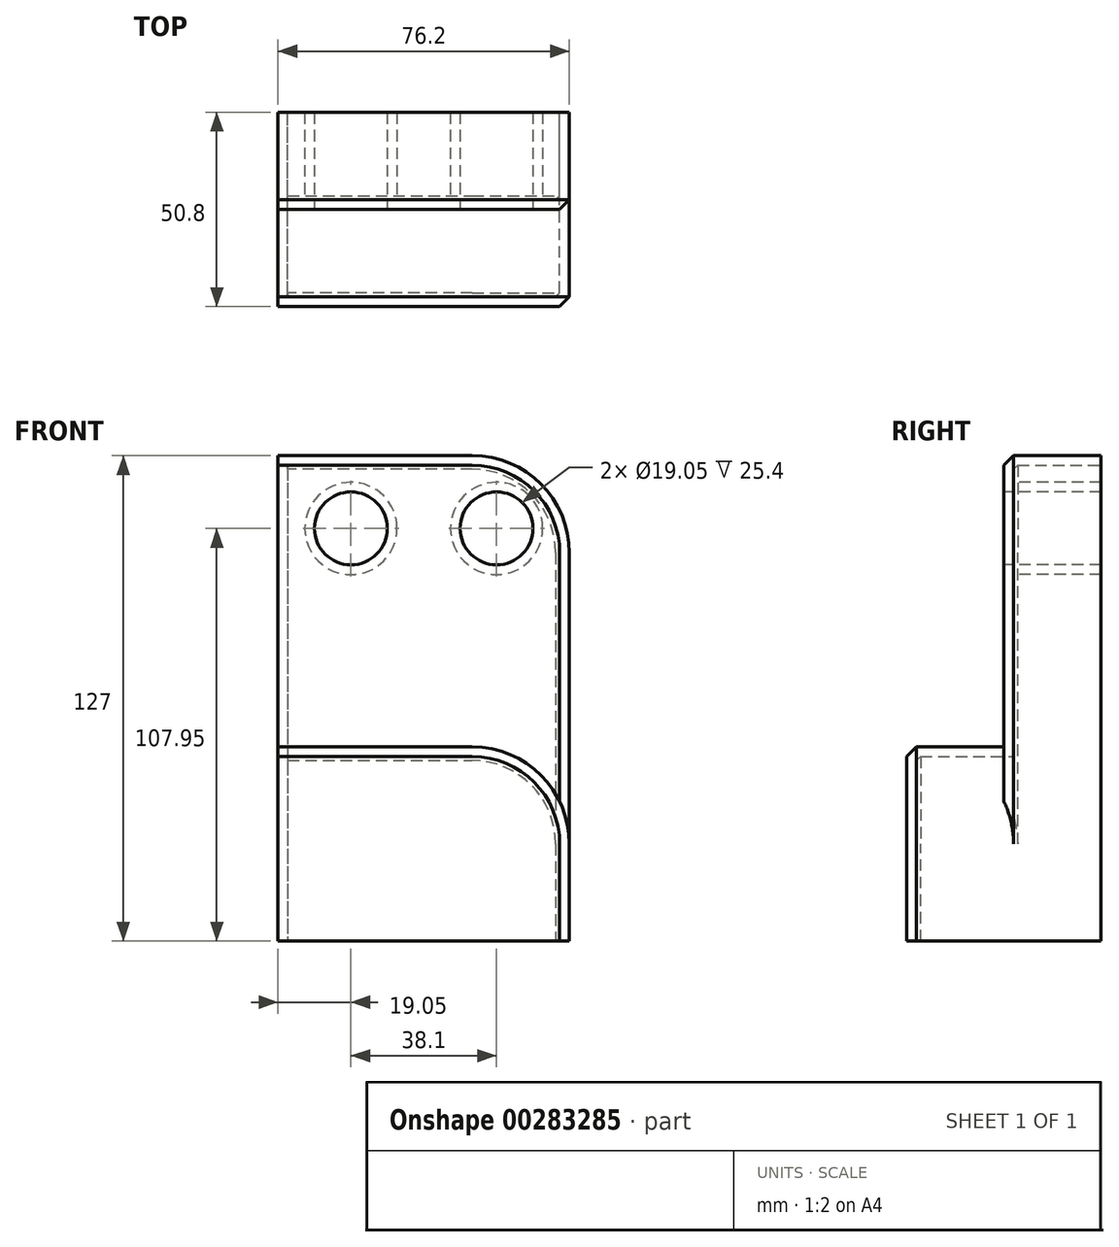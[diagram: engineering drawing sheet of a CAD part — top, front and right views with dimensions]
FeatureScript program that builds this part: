
annotation { "Feature Type Name" : "Feature", "Feature Type Description" : "" }
export const myFeature = defineFeature(function(context is Context, id is Id, definition is map)
    precondition{}
    {
        {
            var Q0;
            Q0=qCreatedBy(makeId("Front.planeOp"),FACE);
            var sketch = newSketch(context, id + "F0", { "sketchPlane" : qUnion([Q0])});
            skLineSegment(sketch, "E0.bottom", {"start": v(38.1, 63.5) * mm, "end": v(-38.1, 63.5) * mm});
            skLineSegment(sketch, "E0.top", {"start": v(38.1, -63.5) * mm, "end": v(-38.1, -63.5) * mm});
            skLineSegment(sketch, "E0.left", {"start": v(38.1, 63.5) * mm, "end": v(38.1, -63.5) * mm});
            skLineSegment(sketch, "E0.right", {"start": v(-38.1, 63.5) * mm, "end": v(-38.1, -63.5) * mm});
            skPoint(sketch, "E0.middle", {"position": v(0, 0) * mm});
            skPoint(sketch, "E1.middle", {"position": v(13.58, 63.5) * mm});
            skSolve(sketch);
        }
        {
            var Q0;
            Q0=makeQuery(id+"F0.imprint","IMPRINT",FACE,{"disambiguationData":[TD([[makeQuery(id+"F0.imprint","IMPRINT",EDGE,{"derivedFrom":sQuery(id+"F0.wireOp",EDGE,"E0.bottom")}),1.0]])]});
            extrude(context, id + "F1", {"entities" : qUnion([Q0]), "depth" : 25.4 * mm});
        }
        {
            var Q0;
            Q0=makeQuery(id+"F1.opExtrude","CAP_FACE",FACE,{"disambiguationData":[OSD([sQuery(id+"F0.wireOp",EDGE,"E0.bottom"),sQuery(id+"F0.wireOp",EDGE,"E0.top"),sQuery(id+"F0.wireOp",EDGE,"E0.left"),sQuery(id+"F0.wireOp",EDGE,"E0.right")])],"isStart":false});
            var sketch = newSketch(context, id + "F2", { "sketchPlane" : qUnion([Q0])});
            skLineSegment(sketch, "E2.bottom", {"start": v(-38.1, -12.7) * mm, "end": v(38.1, -12.7) * mm});
            skLineSegment(sketch, "E2.top", {"start": v(-38.1, -63.5) * mm, "end": v(38.1, -63.5) * mm});
            skLineSegment(sketch, "E2.left", {"start": v(-38.1, -12.7) * mm, "end": v(-38.1, -63.5) * mm});
            skLineSegment(sketch, "E2.right", {"start": v(38.1, -12.7) * mm, "end": v(38.1, -63.5) * mm});
            skSolve(sketch);
        }
        {
            var Q0;
            Q0=makeQuery(id+"F2.imprint","IMPRINT",FACE,{"disambiguationData":[TD([[makeQuery(id+"F2.imprint","IMPRINT",EDGE,{"derivedFrom":sQuery(id+"F2.wireOp",EDGE,"E2.bottom")}),-1.0]])]});
            extrude(context, id + "F3", {"entities" : qUnion([Q0]), "operationType" : NewBodyOperationType.ADD, "depth" : 25.4 * mm});
        }
        {
            var Q0;
            Q0=makeQuery(id+"F1.opExtrude","CAP_FACE",FACE,{"disambiguationData":[OSD([sQuery(id+"F0.wireOp",EDGE,"E0.bottom"),sQuery(id+"F0.wireOp",EDGE,"E0.top"),sQuery(id+"F0.wireOp",EDGE,"E0.left"),sQuery(id+"F0.wireOp",EDGE,"E0.right")])],"isStart":false});
            var sketch = newSketch(context, id + "F4", { "sketchPlane" : qUnion([Q0])});
            skCircle(sketch, "E3", {"center": v(-19.05, 44.45) * mm, "radius": 9.53 * mm});
            skCircle(sketch, "E4", {"center": v(19.05, 44.45) * mm, "radius": 9.53 * mm});
            skSolve(sketch);
        }
        {
            var Q0;
            Q0=sQuery(id+"F4.wireOp",VERTEX,"E3.center");
            var Q1;
            Q1=sQuery(id+"F4.wireOp",VERTEX,"E4.center");
            var Q2;
            Q2=makeQuery(id+"F1.opExtrude","SWEPT_BODY",BODY,{"disambiguationData":[OSD([sQuery(id+"F0.wireOp",EDGE,"E0.bottom"),sQuery(id+"F0.wireOp",EDGE,"E0.top"),sQuery(id+"F0.wireOp",EDGE,"E0.left"),sQuery(id+"F0.wireOp",EDGE,"E0.right")])]});
            hole(context, id + "F5", {"style" : HoleStyle.SIMPLE, "endStyle" : HoleEndStyle.THROUGH, "holeDiameter" : 19.05 * mm, "tappedDepth" : 12.7 * mm, "tapClearance" : 3, "locations" : qUnion([Q0, Q1]), "scope" : qUnion([Q2])});
        }
        {
            var Q0;
            Q0=makeQuery(id+"F1.opExtrude","SWEPT_EDGE",EDGE,{"disambiguationData":[OSD([sQuery(id+"F0.wireOp",EDGE,"E0.bottom"),sQuery(id+"F0.wireOp",EDGE,"E0.left")])]});
            var Q1;
            Q1=makeQuery(id+"F3.opExtrude","SWEPT_EDGE",EDGE,{"disambiguationData":[OSD([sQuery(id+"F0.wireOp",EDGE,"E0.left"),sQuery(id+"F2.wireOp",EDGE,"E2.bottom"),sQuery(id+"F2.wireOp",EDGE,"E2.right")])]});
            fillet(context, id + "F6", {"entities" : qUnion([Q0, Q1]), "radius" : 25.4 * mm, "tangentPropagation" : true, "allowEdgeOverflow" : false});
        }
        {
            var Q0;
            Q0=makeQuery(id+"F1.opExtrude","CAP_EDGE",EDGE,{"disambiguationData":[OSD([sQuery(id+"F0.wireOp",EDGE,"E0.bottom")])],"isStart":false});
            var Q1;
            Q1=makeQuery(id+"F3.opExtrude","CAP_EDGE",EDGE,{"disambiguationData":[OSD([sQuery(id+"F2.wireOp",EDGE,"E2.bottom")])],"isStart":false});
            chamfer(context, id + "F7", {"entities" : qUnion([Q0, Q1]), "width" : 2.54 * mm, "tangentPropagation" : true});
        }
        {
            var Q0;
            Q0=makeQuery(id+"F3.boolean.opBoolean","MERGE",FACE,{"derivedFrom":[makeQuery(id+"F1.opExtrude","SWEPT_FACE",FACE,{"disambiguationData":[OSD([sQuery(id+"F0.wireOp",EDGE,"E0.top")])]}),makeQuery(id+"F3.opExtrude","SWEPT_FACE",FACE,{"disambiguationData":[OSD([sQuery(id+"F2.wireOp",EDGE,"E2.top")])]})]});
            var Q1;
            Q1=makeQuery(id+"F1.opExtrude","CAP_FACE",FACE,{"disambiguationData":[OSD([sQuery(id+"F0.wireOp",EDGE,"E0.bottom"),sQuery(id+"F0.wireOp",EDGE,"E0.top"),sQuery(id+"F0.wireOp",EDGE,"E0.left"),sQuery(id+"F0.wireOp",EDGE,"E0.right")])],"isStart":true});
            shell(context, id + "F8", {"entities" : qUnion([Q0, Q1]), "thickness" : 2.54 * mm});
        }
    });
